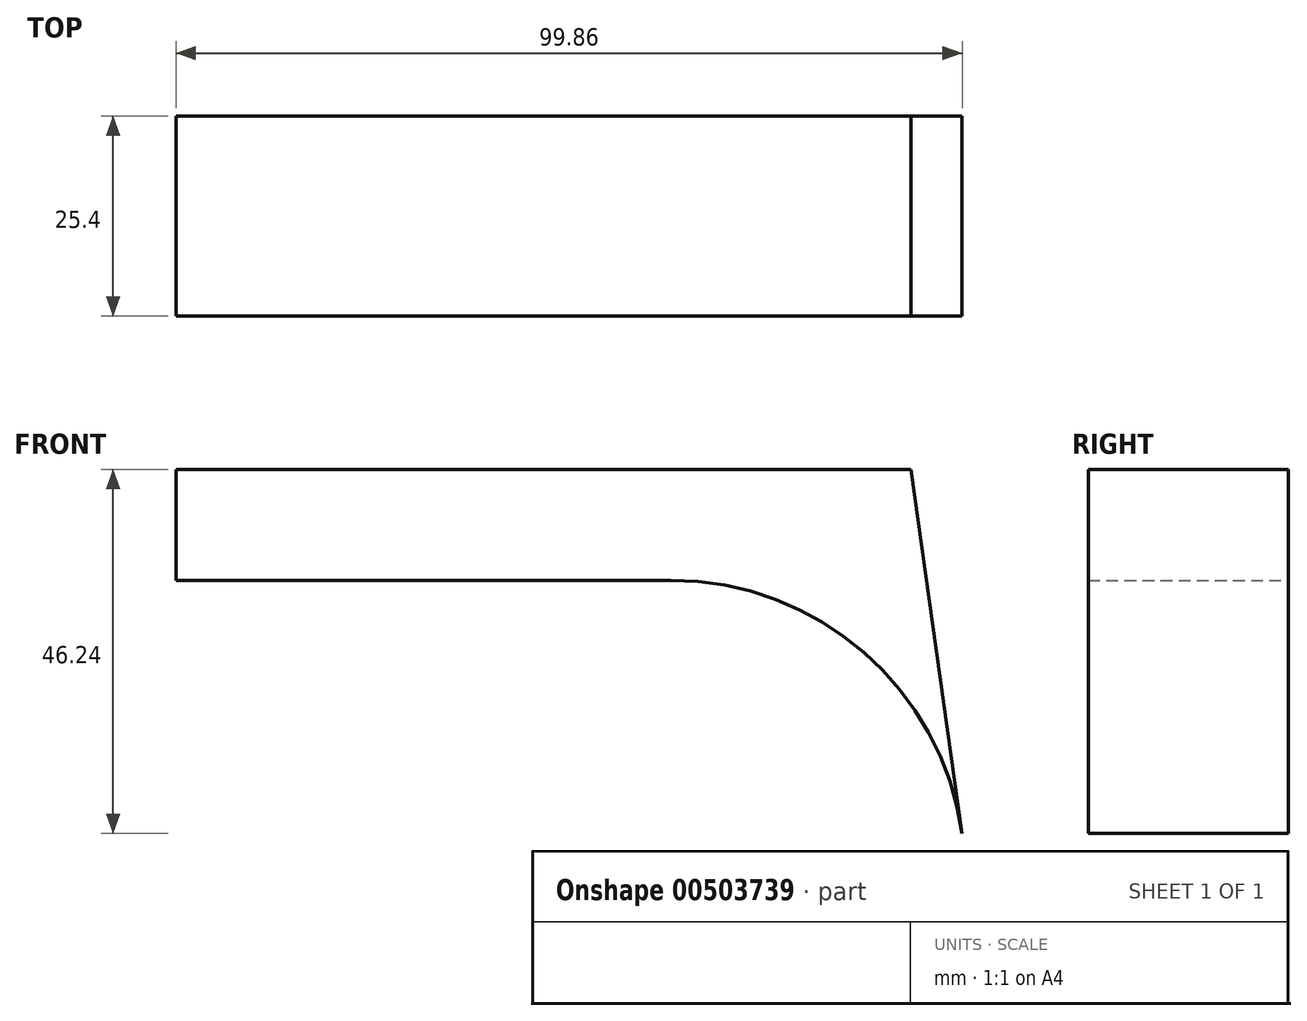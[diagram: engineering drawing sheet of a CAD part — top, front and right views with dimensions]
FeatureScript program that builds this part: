
annotation { "Feature Type Name" : "Feature", "Feature Type Description" : "" }
export const myFeature = defineFeature(function(context is Context, id is Id, definition is map)
    precondition{}
    {
        {
            var Q0;
            Q0=qCreatedBy(makeId("Front.planeOp"),FACE);
            var sketch = newSketch(context, id + "F0", { "sketchPlane" : qUnion([Q0])});
            skCircle(sketch, "E0", {"center": v(0, 0) * mm, "radius": 37.38 * mm});
            skCircle(sketch, "E1", {"center": v(0, 0) * mm, "radius": 14.36 * mm});
            skLineSegment(sketch, "E2", {"start": v(0, 37.38) * mm, "end": v(-62.84, 37.38) * mm});
            skLineSegment(sketch, "E3", {"start": v(-62.84, 37.38) * mm, "end": v(-62.84, 51.45) * mm});
            skLineSegment(sketch, "E4", {"start": v(-62.84, 51.45) * mm, "end": v(30.51, 51.45) * mm});
            skLineSegment(sketch, "E5", {"start": v(30.51, 51.45) * mm, "end": v(37.02, 5.2) * mm});
            skSolve(sketch);
        }
        {
            var Q0;
            {var subQ0=sQuery(id+"F0.wireOp",EDGE,"E2");Q0=makeQuery(id+"F0.imprint","IMPRINT",FACE,{"disambiguationData":[TD([[makeQuery(id+"F0.imprint","IMPRINT",EDGE,{"derivedFrom":subQ0}),-1.0]])]});}
            extrude(context, id + "F1", {"entities" : qUnion([Q0]), "depth" : 25.4 * mm});
        }
    });
